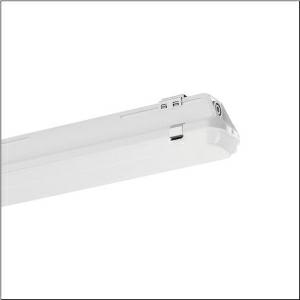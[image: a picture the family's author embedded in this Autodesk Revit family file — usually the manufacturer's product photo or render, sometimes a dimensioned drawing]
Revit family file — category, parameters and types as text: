
# Revit family: monsun_r__12_51fp108p430h_3720
name_source: partatom
category: Lighting Fixtures
units: mm (PartAtom-declared; Revit-internal decimal feet)

## family parameters
Cut with Voids When Loaded = No
Host = Face
Light Source = No
Part Type = Normal
Room Calculation Point = No
Round Connector Dimension = Use Diameter
Shared = No

## types (1)
- Monsun® 12 (1 x LED, 3970 lm, 22.2 W, 4000K)
    Apparent Load = 22 VA
    CIE Flux Codes = 47 77 93 94 100
    Color Rendering = 80
    Color Temperature = 4000K
    Default Elevation = 1800 mm
    Description = Monsun® 12, damp-proof luminaire, chain hanger, primary optical cover: enclosure, of PMMA, light emission: direct distribution, primary light characteristic: symmetric, installation type: suspended mounting, surface-mounted, horizontal mounting, vertical mounting, LED rated luminous flux: 3.970 lm, light colour: 840, colour temperature: 4000K, control gear: ECG, with terminal, 3-pole, max. 2.5mm², mains connection: 220..240V, AC, 50/60Hz, rated input power: 22W, luminaire housing, of glass-fibre reinforced polyester, uncoated, bright grey, length: 1.590 mm, width: 90 mm, height: 88mm, clip for enclosure, of stainless steel (V2A), ceiling mounting element, of stainless steel (V2A), chain hanger, of stainless steel (V2A), protection rating (complete): IP66, insulation class (complete): insulation class I (protective earthing), certification: CE, ENEC, VDE, protection symbol: D, impact resistance: IK04, permissible ambient temperature for indoor applications: -35..+40°C, standard: EN 50419, EN 60598-2-1, no direct snow, no direct sun, no direct rain, for indoor or canopied outdoor use, corresponds to IFS (International Featured Standards) requirements for safety and quality in the food industry, for animal farming (ammonia tested): for use in cowhouse, pig house, horse-stables... (not for use in poultry stables), AT max for animal farming = 40°C, packaging unit: 1 piece
    Height = 89 mm
    Lamp = 1 x LED
    Lamp Light Flux = 3970 lm
    Lamp Power = 22.2 W
    Lamp count = 1
    Length = 1590 mm
    Luminous efficacy = 179 lm/W
    Manufacturer = Siteco
    ModVariant = No
    Model = 51FP108P430H
    Mounting Place = Ceiling
    Mounting Type = Pendant
    Number of Poles = 1
    OnlyDefault = Yes
    Power Factor = 1
    Product Name = Monsun® 12
    Product group = damp-proof luminaire | ceiling pendant
    ProductGroupID = 908
    Protection Class = Protection class I
    Protection Degree = IP 66
    RLX_Detail_Level = 1
    RlxData = <blob elided: 88225 chars, md5=4fdd434b>
    Socket = socket
    Standby Power = 0 W
    System Light Flux = 3970 lm
    System Power = 22 W
    Type Comments = Product without accessories
    Type Image = l_1004748.jpg
    URL = http://relux.com
    VarID = ---
    Voltage = 0 V
    Weight = 0.00 kg
    Width = 90 mm

## geometry (parser evidence)
native form markers: Blend x4, Sweep x12
no freeform markers — native parametric forms only
